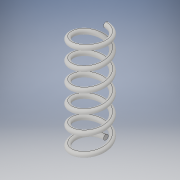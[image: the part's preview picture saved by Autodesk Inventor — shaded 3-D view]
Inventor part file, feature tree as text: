
AUTODESK INVENTOR PART (.ipt)
format: ipt  version: 2019 (Build 230136000, 136)  size: 474,112 bytes
history: native  units: in
note: dims shown in document units (in); Inventor stores cm internally (conversion verified against a paired STEP export)
features: helix x1, sketch x1
ambient origin geometry x8: Origin, YZ Plane, XZ Plane, XY Plane, X Axis, Y Axis, Z Axis, Center Point
bodies: Solid1 (feature_tree)
feature tree (2):
  helix  "Coil1"  [1 undecoded]
  sketch  "Sketch1"  dims[d1=0.0787in d2=1.7717in d3=0.3937in d4=1.5748in d5=1.9685in d6=0.0in d7=90.0deg d8=90.0deg d9=90.0deg d10=90.0deg]
note: 1 required parameter value undecoded (feature->parameter linkage not recoverable at this tier; creation-order binding heuristic only, values carry confidence <= 0.55)
